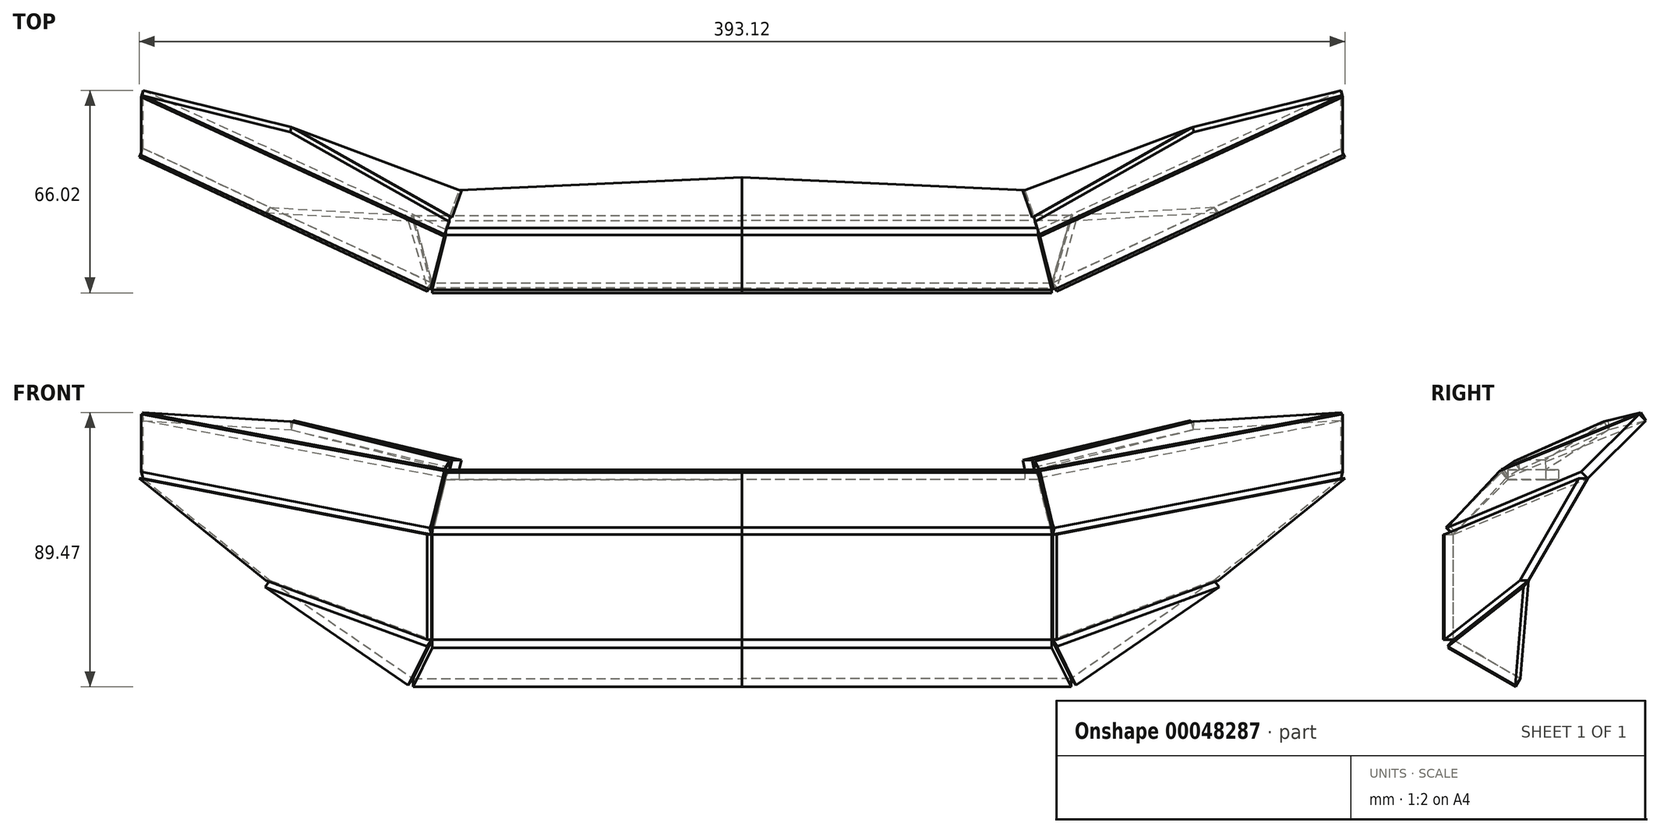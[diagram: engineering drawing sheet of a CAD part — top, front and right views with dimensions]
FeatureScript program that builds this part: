
annotation { "Feature Type Name" : "Feature", "Feature Type Description" : "" }
export const myFeature = defineFeature(function(context is Context, id is Id, definition is map)
    precondition{}
    {
        {
            var Q0;
            Q0=qCreatedBy(makeId("Front.planeOp"),FACE);
            var sketch = newSketch(context, id + "F0", { "sketchPlane" : qUnion([Q0])});
            skLineSegment(sketch, "E0.bottom", {"start": v(0, 14.98) * mm, "end": v(-100.98, 14.98) * mm});
            skLineSegment(sketch, "E0.top", {"start": v(0, -19.25) * mm, "end": v(-100.98, -19.25) * mm});
            skLineSegment(sketch, "E0.left", {"start": v(0, 14.98) * mm, "end": v(0, -19.25) * mm});
            skLineSegment(sketch, "E0.right", {"start": v(-100.98, 14.98) * mm, "end": v(-100.98, -19.25) * mm});
            skSolve(sketch);
        }
        {
            var Q0;
            Q0=makeQuery(id+"F0.imprint","IMPRINT",FACE,{"disambiguationData":[TD([[makeQuery(id+"F0.imprint","IMPRINT",EDGE,{"derivedFrom":sQuery(id+"F0.wireOp",EDGE,"E0.bottom")}),1.0]])]});
            extrude(context, id + "F1", {"entities" : qUnion([Q0]), "depth" : 3.17 * mm});
        }
        {
            var Q0;
            Q0=makeQuery(id+"F1.opExtrude","CAP_EDGE",EDGE,{"disambiguationData":[OSD([sQuery(id+"F0.wireOp",EDGE,"E0.right")])],"isStart":true});
            cPlane(context, id + "F2", {"entities" : qUnion([Q0]), "cplaneType" : CPlaneType.LINE_ANGLE, "offset" : 152.4 * mm, "angle" : 115 * degree, "width" : 152.4 * mm, "height" : 152.4 * mm});
        }
        {
            var Q0;
            Q0=qCreatedBy(id+"F2.planeOp",FACE);
            var sketch = newSketch(context, id + "F3", { "sketchPlane" : qUnion([Q0])});
            skLineSegment(sketch, "E1", {"start": v(91.52, 14.98) * mm, "end": v(91.52, -19.25) * mm});
            skLineSegment(sketch, "E2", {"start": v(91.83, 14.98) * mm, "end": v(195.5, 33.26) * mm});
            skLineSegment(sketch, "E3", {"start": v(195.5, 33.26) * mm, "end": v(149.9, 0) * mm});
            skLineSegment(sketch, "E4", {"start": v(149.9, 0) * mm, "end": v(91.83, -19.25) * mm});
            skLineSegment(sketch, "E5", {"start": v(91.83, -19.25) * mm, "end": v(91.83, 14.98) * mm});
            skSolve(sketch);
        }
        {
            var Q0;
            Q0 = qSketchRegion(id + "F3", true);
            extrude(context, id + "F4", {"entities" : qUnion([Q0]), "oppositeDirection" : true, "depth" : 3.17 * mm});
        }
        {
            var Q0;
            Q0=makeQuery(id+"F1.opExtrude","CAP_EDGE",EDGE,{"disambiguationData":[OSD([sQuery(id+"F0.wireOp",EDGE,"E0.bottom")])],"isStart":true});
            cPlane(context, id + "F5", {"entities" : qUnion([Q0]), "cplaneType" : CPlaneType.LINE_ANGLE, "offset" : 152.4 * mm, "angle" : 45 * degree, "width" : 152.4 * mm, "height" : 152.4 * mm});
        }
        {
            var Q0;
            Q0=qCreatedBy(id+"F5.planeOp",FACE);
            var sketch = newSketch(context, id + "F6", { "sketchPlane" : qUnion([Q0])});
            skLineSegment(sketch, "E6", {"start": v(-100.98, 10.59) * mm, "end": v(0, 10.59) * mm});
            skLineSegment(sketch, "E7", {"start": v(-100.98, 10.59) * mm, "end": v(-96.52, 35.99) * mm});
            skLineSegment(sketch, "E8", {"start": v(-96.52, 35.99) * mm, "end": v(0, 35.99) * mm});
            skLineSegment(sketch, "E9", {"start": v(0, 35.99) * mm, "end": v(0, 10.59) * mm});
            skSolve(sketch);
        }
        {
            var Q0;
            Q0=makeQuery(id+"F4.opExtrude","CAP_EDGE",EDGE,{"disambiguationData":[OSD([sQuery(id+"F3.wireOp",EDGE,"E2")])],"isStart":true});
            cPlane(context, id + "F7", {"entities" : qUnion([Q0]), "cplaneType" : CPlaneType.LINE_ANGLE, "offset" : 152.4 * mm, "angle" : 45 * degree, "width" : 152.4 * mm, "height" : 152.4 * mm});
        }
        {
            var Q0;
            Q0=makeQuery(id+"F6.imprint","IMPRINT",FACE,{"disambiguationData":[TD([[makeQuery(id+"F6.imprint","IMPRINT",EDGE,{"derivedFrom":sQuery(id+"F6.wireOp",EDGE,"E6")}),1.0]])]});
            extrude(context, id + "F8", {"entities" : qUnion([Q0]), "depth" : 3.17 * mm});
        }
        {
            var Q0;
            Q0=makeQuery(id+"F1.opExtrude","CAP_EDGE",EDGE,{"disambiguationData":[OSD([sQuery(id+"F0.wireOp",EDGE,"E0.top")])],"isStart":true});
            cPlane(context, id + "F9", {"entities" : qUnion([Q0]), "cplaneType" : CPlaneType.LINE_ANGLE, "offset" : 152.4 * mm, "angle" : 120 * degree, "width" : 152.4 * mm, "height" : 152.4 * mm});
        }
        {
            var Q0;
            Q0=qCreatedBy(id+"F9.planeOp",FACE);
            var sketch = newSketch(context, id + "F10", { "sketchPlane" : qUnion([Q0])});
            skLineSegment(sketch, "E10", {"start": v(0, 9.63) * mm, "end": v(-100.98, 9.63) * mm});
            skLineSegment(sketch, "E11", {"start": v(-100.98, 9.63) * mm, "end": v(-107.25, 35.03) * mm});
            skLineSegment(sketch, "E12", {"start": v(-107.25, 35.03) * mm, "end": v(0, 35.03) * mm});
            skLineSegment(sketch, "E13", {"start": v(0, 35.03) * mm, "end": v(0, 9.63) * mm});
            skSolve(sketch);
        }
        {
            var Q0;
            Q0=makeQuery(id+"F10.imprint","IMPRINT",FACE,{"disambiguationData":[TD([[makeQuery(id+"F10.imprint","IMPRINT",EDGE,{"derivedFrom":sQuery(id+"F10.wireOp",EDGE,"E10")}),-1.0]])]});
            extrude(context, id + "F11", {"entities" : qUnion([Q0]), "oppositeDirection" : true, "depth" : 3.17 * mm});
        }
        {
            var Q0;
            Q0=makeQuery(id+"F4.opExtrude","CAP_VERTEX",VERTEX,{"disambiguationData":[OSD([sQuery(id+"F3.wireOp",EDGE,"E3"),sQuery(id+"F3.wireOp",EDGE,"E4")])],"isStart":true});
            var Q1;
            Q1=makeQuery(id+"F4.opExtrude","CAP_VERTEX",VERTEX,{"disambiguationData":[OSD([sQuery(id+"F3.wireOp",EDGE,"E4"),sQuery(id+"F3.wireOp",EDGE,"E5")])],"isStart":true});
            var Q2;
            Q2=makeQuery(id+"F11.opExtrude","CAP_VERTEX",VERTEX,{"disambiguationData":[OSD([sQuery(id+"F10.wireOp",EDGE,"E11"),sQuery(id+"F10.wireOp",EDGE,"E12")])],"isStart":true});
            cPlane(context, id + "F12", {"entities" : qUnion([Q0, Q1, Q2]), "cplaneType" : CPlaneType.THREE_POINT, "offset" : 152.4 * mm, "width" : 152.4 * mm, "height" : 152.4 * mm});
        }
        {
            var Q0;
            Q0=qCreatedBy(id+"F12.planeOp",FACE);
            var sketch = newSketch(context, id + "F13", { "sketchPlane" : qUnion([Q0])});
            skLineSegment(sketch, "E14", {"start": v(-87.16, -37) * mm, "end": v(-79.93, -11.86) * mm});
            skLineSegment(sketch, "E15", {"start": v(-80.24, -11.95) * mm, "end": v(-140.97, -19.45) * mm});
            skLineSegment(sketch, "E16", {"start": v(-140.97, -19.45) * mm, "end": v(-87.16, -37) * mm});
            skLineSegment(sketch, "E17", {"start": v(-79.93, -11.86) * mm, "end": v(-80.24, -11.95) * mm});
            skSolve(sketch);
        }
        {
            var Q0;
            Q0 = qSketchRegion(id + "F13", true);
            extrude(context, id + "F14", {"entities" : qUnion([Q0]), "depth" : 3.17 * mm});
        }
        {
            var Q0;
            Q0=qCreatedBy(id+"F7.planeOp",FACE);
            var sketch = newSketch(context, id + "F15", { "sketchPlane" : qUnion([Q0])});
            skLineSegment(sketch, "E18", {"start": v(-92.67, 35.96) * mm, "end": v(-96.99, 11.8) * mm});
            skLineSegment(sketch, "E19", {"start": v(-193.15, 54.6) * mm, "end": v(-97.49, 10.65) * mm});
            skLineSegment(sketch, "E20", {"start": v(-193.15, 54.6) * mm, "end": v(-193.15, 81.28) * mm});
            skLineSegment(sketch, "E21", {"start": v(-193.15, 81.28) * mm, "end": v(-92.67, 35.96) * mm});
            skLineSegment(sketch, "E22", {"start": v(-97.49, 10.65) * mm, "end": v(-96.99, 11.8) * mm});
            skSolve(sketch);
        }
        {
            var Q0;
            Q0 = qSketchRegion(id + "F15", true);
            extrude(context, id + "F16", {"entities" : qUnion([Q0]), "depth" : 3.17 * mm});
        }
        {
            var Q0;
            Q0=makeQuery(id+"F8.opExtrude","CAP_EDGE",EDGE,{"disambiguationData":[OSD([sQuery(id+"F6.wireOp",EDGE,"E8")])],"isStart":true});
            cPlane(context, id + "F17", {"entities" : qUnion([Q0]), "cplaneType" : CPlaneType.LINE_ANGLE, "offset" : 152.4 * mm, "angle" : 90 * degree, "width" : 152.4 * mm, "height" : 152.4 * mm});
        }
        {
            var Q0;
            Q0=qCreatedBy(id+"F17.planeOp",FACE);
            var sketch = newSketch(context, id + "F18", { "sketchPlane" : qUnion([Q0])});
            skLineSegment(sketch, "E23", {"start": v(0, 17.96) * mm, "end": v(-96.52, 17.96) * mm});
            skLineSegment(sketch, "E24", {"start": v(-96.52, 17.96) * mm, "end": v(-92.19, 30.28) * mm});
            skLineSegment(sketch, "E25", {"start": v(-92.19, 30.28) * mm, "end": v(0, 34.46) * mm});
            skLineSegment(sketch, "E26", {"start": v(0, 34.46) * mm, "end": v(0, 17.96) * mm});
            skSolve(sketch);
        }
        {
            var Q0;
            Q0 = qSketchRegion(id + "F18", true);
            extrude(context, id + "F19", {"entities" : qUnion([Q0]), "depth" : 3.17 * mm});
        }
        {
            var Q0;
            Q0=makeQuery(id+"F16.opExtrude","CAP_EDGE",EDGE,{"disambiguationData":[OSD([sQuery(id+"F15.wireOp",EDGE,"E21")])],"isStart":true});
            cPlane(context, id + "F20", {"entities" : qUnion([Q0]), "cplaneType" : CPlaneType.LINE_ANGLE, "offset" : 152.4 * mm, "angle" : 120 * degree, "width" : 152.4 * mm, "height" : 152.4 * mm});
        }
        {
            var Q0;
            Q0=qCreatedBy(id+"F20.planeOp",FACE);
            var sketch = newSketch(context, id + "F21", { "sketchPlane" : qUnion([Q0])});
            skLineSegment(sketch, "E27", {"start": v(-93.45, 37.18) * mm, "end": v(-94.74, 32.84) * mm});
            skLineSegment(sketch, "E28", {"start": v(-94.74, 32.22) * mm, "end": v(-193.73, 80.71) * mm});
            skLineSegment(sketch, "E29", {"start": v(-193.73, 80.71) * mm, "end": v(-145.34, 68.9) * mm});
            skLineSegment(sketch, "E30", {"start": v(-145.34, 68.9) * mm, "end": v(-93.45, 37.18) * mm});
            skLineSegment(sketch, "E31", {"start": v(-94.74, 32.84) * mm, "end": v(-94.74, 32.22) * mm});
            skSolve(sketch);
        }
        {
            var Q0;
            Q0=makeQuery(id+"F21.imprint","IMPRINT",FACE,{"disambiguationData":[TD([[makeQuery(id+"F21.imprint","IMPRINT",EDGE,{"derivedFrom":sQuery(id+"F21.wireOp",EDGE,"E27")}),-1.0]])]});
            extrude(context, id + "F22", {"entities" : qUnion([Q0]), "operationType" : NewBodyOperationType.ADD, "depth" : 3.17 * mm});
        }
        {
            var Q0;
            Q0=makeQuery(id+"F19.opExtrude","CAP_VERTEX",VERTEX,{"disambiguationData":[OSD([sQuery(id+"F18.wireOp",EDGE,"E24"),sQuery(id+"F18.wireOp",EDGE,"E25")])],"isStart":false});
            var Q1;
            Q1=makeQuery(id+"F22.opExtrude","CAP_VERTEX",VERTEX,{"disambiguationData":[OSD([sQuery(id+"F21.wireOp",EDGE,"E27"),sQuery(id+"F21.wireOp",EDGE,"E30")])],"isStart":true});
            var Q2;
            Q2=makeQuery(id+"F22.opExtrude","CAP_VERTEX",VERTEX,{"disambiguationData":[OSD([sQuery(id+"F21.wireOp",EDGE,"E29"),sQuery(id+"F21.wireOp",EDGE,"E30")])],"isStart":true});
            cPlane(context, id + "F23", {"entities" : qUnion([Q0, Q1, Q2]), "cplaneType" : CPlaneType.THREE_POINT, "offset" : 152.4 * mm, "width" : 152.4 * mm, "height" : 152.4 * mm});
        }
        {
            var Q0;
            Q0=qCreatedBy(id+"F23.planeOp",FACE);
            var sketch = newSketch(context, id + "F24", { "sketchPlane" : qUnion([Q0])});
            skLineSegment(sketch, "E32", {"start": v(-97.15, 32.85) * mm, "end": v(-100.26, 24.22) * mm});
            skLineSegment(sketch, "E33", {"start": v(-100.26, 24.22) * mm, "end": v(-153.12, 54.3) * mm});
            skLineSegment(sketch, "E34", {"start": v(-153.12, 54.3) * mm, "end": v(-97.15, 32.85) * mm});
            skSolve(sketch);
        }
        {
            var Q0;
            Q0=makeQuery(id+"F24.imprint","IMPRINT",FACE,{"disambiguationData":[TD([[makeQuery(id+"F24.imprint","IMPRINT",EDGE,{"derivedFrom":sQuery(id+"F24.wireOp",EDGE,"E32")}),-1.0]])]});
            extrude(context, id + "F25", {"entities" : qUnion([Q0]), "depth" : 3.17 * mm});
        }
        {
            var Q0;
            Q0=makeQuery(id+"F25.opExtrude","SWEPT_BODY",BODY,{"disambiguationData":[OSD([sQuery(id+"F24.wireOp",EDGE,"E32"),sQuery(id+"F24.wireOp",EDGE,"E33"),sQuery(id+"F24.wireOp",EDGE,"E34")])]});
            var Q1;
            Q1=makeQuery(id+"F4.opExtrude","SWEPT_BODY",BODY,{"disambiguationData":[OSD([sQuery(id+"F3.wireOp",EDGE,"E2"),sQuery(id+"F3.wireOp",EDGE,"E3"),sQuery(id+"F3.wireOp",EDGE,"E4"),sQuery(id+"F3.wireOp",EDGE,"E5")])]});
            var Q2;
            Q2=makeQuery(id+"F14.opExtrude","SWEPT_BODY",BODY,{"disambiguationData":[OSD([sQuery(id+"F13.wireOp",EDGE,"E14"),sQuery(id+"F13.wireOp",EDGE,"E15"),sQuery(id+"F13.wireOp",EDGE,"E16"),sQuery(id+"F13.wireOp",EDGE,"E17")])]});
            var Q3;
            Q3=makeQuery(id+"F11.opExtrude","SWEPT_BODY",BODY,{"disambiguationData":[OSD([sQuery(id+"F10.wireOp",EDGE,"E10"),sQuery(id+"F10.wireOp",EDGE,"E11"),sQuery(id+"F10.wireOp",EDGE,"E12"),sQuery(id+"F10.wireOp",EDGE,"E13")])]});
            var Q4;
            Q4=makeQuery(id+"F1.opExtrude","SWEPT_BODY",BODY,{"disambiguationData":[OSD([sQuery(id+"F0.wireOp",EDGE,"E0.bottom"),sQuery(id+"F0.wireOp",EDGE,"E0.top"),sQuery(id+"F0.wireOp",EDGE,"E0.left"),sQuery(id+"F0.wireOp",EDGE,"E0.right")])]});
            var Q5;
            Q5=makeQuery(id+"F8.opExtrude","SWEPT_BODY",BODY,{"disambiguationData":[OSD([sQuery(id+"F6.wireOp",EDGE,"E6"),sQuery(id+"F6.wireOp",EDGE,"E7"),sQuery(id+"F6.wireOp",EDGE,"E8"),sQuery(id+"F6.wireOp",EDGE,"E9")])]});
            var Q6;
            Q6=makeQuery(id+"F16.opExtrude","SWEPT_BODY",BODY,{"disambiguationData":[OSD([sQuery(id+"F15.wireOp",EDGE,"E18"),sQuery(id+"F15.wireOp",EDGE,"E19"),sQuery(id+"F15.wireOp",EDGE,"E20"),sQuery(id+"F15.wireOp",EDGE,"E21"),sQuery(id+"F15.wireOp",EDGE,"E22")])]});
            var Q7;
            Q7=makeQuery(id+"F19.opExtrude","SWEPT_BODY",BODY,{"disambiguationData":[OSD([sQuery(id+"F18.wireOp",EDGE,"E23"),sQuery(id+"F18.wireOp",EDGE,"E24"),sQuery(id+"F18.wireOp",EDGE,"E25"),sQuery(id+"F18.wireOp",EDGE,"E26")])]});
            var Q8;
            Q8=qCreatedBy(makeId("Right.planeOp"),FACE);
            mirror(context, id + "F26", {"entities" : qUnion([Q0, Q1, Q2, Q3, Q4, Q5, Q6, Q7]), "mirrorPlane" : qUnion([Q8])});
        }
    });
